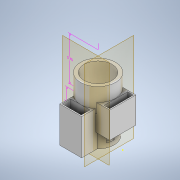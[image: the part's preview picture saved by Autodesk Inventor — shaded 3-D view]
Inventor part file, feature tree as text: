
AUTODESK INVENTOR PART (.ipt)
format: ipt  version: 2021 (Build 250183000, 183)  size: 448,000 bytes
history: native  units: in
note: dims shown in document units (in); Inventor stores cm internally (conversion verified against a paired STEP export)
features: sketch x24, extrude x14, other x3, plane x3, fillet x1
ambient origin geometry x8: Origin, YZ Plane, XZ Plane, XY Plane, X Axis, Y Axis, Z Axis, Center Point
bodies: Solid1 (feature_tree)
feature tree (45):
  other  "Annotations"
  extrude  "Extrusion1"  Depth=3.5433in TaperAngle=0.0deg
  extrude  "Extrusion2"  Depth=5.75in TaperAngle=0.0deg
  sketch  "Sketch4"  dims[d34=5.575in d35=0.0in d58=0.0787in]
  sketch  "Sketch5"  dims[d59=1.25in d60=4.1in]
  sketch  "Sketch6"  dims[d61=1.25in d62=4.1in]
  fillet  "Fillet1"  Radius=3.2in
  plane  "Work Plane2"
  extrude  "Extrusion4"  Depth=0.6875in TaperAngle=0.0deg
  sketch  "Sketch12"  dims[d67=2.2in d68=1.0in]
  sketch  "Sketch13"  dims[d69=3.8625in d70=0.0in d71=1.0in]
  extrude  "Extrusion8"  Depth=0.0787in
  plane  "Work Plane4"
  sketch  "Sketch24"  dims[d74=1.825in d75=0.0in d76=1.25in]
  extrude  "Extrusion13"  Depth=4.1in
  extrude  "Extrusion14"  Depth=4.1in
  sketch  "Sketch27"  dims[d81=1.0in d82=0.0in d83=1.875in d84=0.0in]
  sketch  "Sketch28"  dims[d85=0.65in]
  extrude  "Extrusion15"  Depth=1.7625in TaperAngle=0.0deg
  extrude  "Extrusion16"  Depth=1.0in
  plane  "Work Plane5"
  extrude  "Extrusion17"  Depth=1.0in
  sketch  "Sketch32"  dims[d91=3.0in d92=0.0in]
  extrude  "Extrusion18"  Depth=1.5in
  extrude  "Extrusion3"  Depth=1.25in
  extrude  "Extrusion19"  Depth=1.5in
  sketch  "Sketch35"  dims[d18=0.0344in]
  extrude  "Extrusion20"  Depth=1.5in
  extrude  "Extrusion21"  Depth=1.875in TaperAngle=0.0deg
  sketch  "Sketch1"  dims[d0=3.6614in d1=3.5433in d2=0.0in]
  sketch  "Sketch2"  dims[d3=4.0in d4=5.75in d5=0.0in d6=3.2in]
  sketch  "Sketch3"  dims[d7=9.0in d8=0.0in d11=0.6875in d12=0.0in]
  sketch  "Sketch7"  dims[d63=1.3in d64=0.0in d65=1.7625in d66=0.0in]
  sketch  "Sketch14"  dims[d72=0.6in d73=1.5in]
  sketch  "Sketch25"  dims[d77=3.0in d78=1.5in]
  sketch  "Sketch26"  dims[d79=3.0in d80=1.5in]
  sketch  "Sketch29"  dims[d86=2.7in]
  sketch  "Sketch30"  dims[d87=2.8125in d88=0.0in]
  sketch  "Sketch31"  dims[d89=2.8125in d90=0.0in]
  sketch  "Sketch33"  dims[d10=5.75in d9=3.5433in]
  sketch  "Sketch34"  dims[d17=0.5in]
  sketch  "Sketch36"  dims[d19=0.5in]
  sketch  "Sketch37"  dims[d20=0.0344in]
  other  "Linear Dimension 1"
  other  "Linear Dimension 2"
